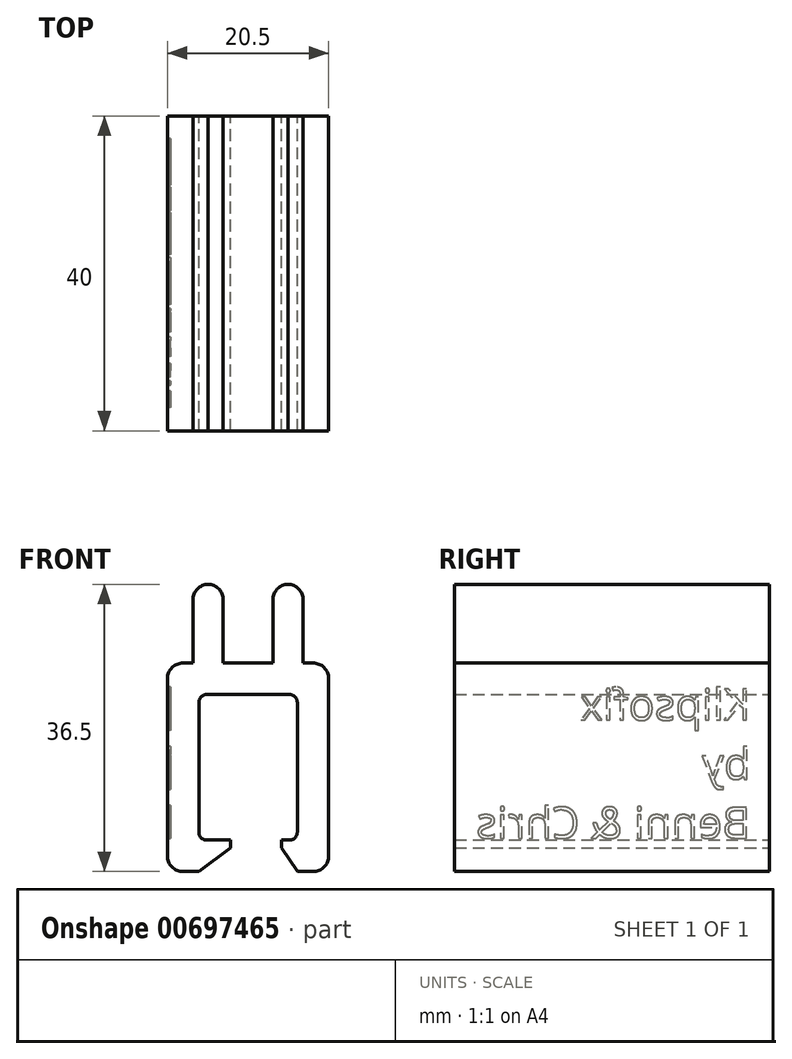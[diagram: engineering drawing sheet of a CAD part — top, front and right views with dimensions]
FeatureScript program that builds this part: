
annotation { "Feature Type Name" : "Feature", "Feature Type Description" : "" }
export const myFeature = defineFeature(function(context is Context, id is Id, definition is map)
    precondition{}
    {
        {
            var Q0;
            Q0=qCreatedBy(makeId("Front.planeOp"),FACE);
            var sketch = newSketch(context, id + "F0", { "sketchPlane" : qUnion([Q0])});
            skLineSegment(sketch, "E0", {"start": v(-16.5, 22.5) * mm, "end": v(-16.5, 4) * mm});
            skLineSegment(sketch, "E1", {"start": v(-16.5, 22.5) * mm, "end": v(-4, 22.5) * mm});
            skLineSegment(sketch, "E2", {"start": v(-4, 22.5) * mm, "end": v(-4, 4) * mm});
            skLineSegment(sketch, "E3", {"start": v(-4, 4) * mm, "end": v(-6, 4) * mm});
            skLineSegment(sketch, "E4", {"start": v(-6, 4) * mm, "end": v(-6, 3) * mm});
            skLineSegment(sketch, "E5", {"start": v(-6, 3) * mm, "end": v(-4, 0) * mm});
            skLineSegment(sketch, "E6", {"start": v(-4, 0) * mm, "end": v(0, 0) * mm});
            skLineSegment(sketch, "E7", {"start": v(0, 0) * mm, "end": v(0, 26.5) * mm});
            skLineSegment(sketch, "E8", {"start": v(0, 26.5) * mm, "end": v(-20.5, 26.5) * mm, "construction": true});
            skLineSegment(sketch, "E9", {"start": v(-20.5, 26.5) * mm, "end": v(-20.5, 0) * mm});
            skLineSegment(sketch, "E10", {"start": v(-20.5, 0) * mm, "end": v(-16.5, 0) * mm});
            skLineSegment(sketch, "E11", {"start": v(-16.5, 4) * mm, "end": v(-12.5, 4) * mm});
            skLineSegment(sketch, "E12", {"start": v(-12.5, 4) * mm, "end": v(-12.5, 3) * mm});
            skLineSegment(sketch, "E13", {"start": v(-12.5, 3) * mm, "end": v(-16.5, 0) * mm});
            skLineSegment(sketch, "E14", {"start": v(-10.25, 26.5) * mm, "end": v(-10.25, 36.5) * mm, "construction": true});
            skLineSegment(sketch, "E15", {"start": v(-13.4, 26.5) * mm, "end": v(-13.4, 36.5) * mm});
            skLineSegment(sketch, "E16", {"start": v(-17.25, 26.5) * mm, "end": v(-17.25, 36.5) * mm});
            skLineSegment(sketch, "E17", {"start": v(-7.1, 26.5) * mm, "end": v(-7.1, 36.5) * mm});
            skLineSegment(sketch, "E18", {"start": v(-3.25, 26.5) * mm, "end": v(-3.25, 36.5) * mm});
            skLineSegment(sketch, "E19", {"start": v(-17.25, 36.5) * mm, "end": v(-13.4, 36.5) * mm});
            skLineSegment(sketch, "E20", {"start": v(-7.1, 36.5) * mm, "end": v(-3.25, 36.5) * mm});
            skLineSegment(sketch, "E21", {"start": v(-13.4, 26.5) * mm, "end": v(-7.1, 26.5) * mm});
            skLineSegment(sketch, "E22", {"start": v(-3.25, 26.5) * mm, "end": v(0, 26.5) * mm});
            skLineSegment(sketch, "E23", {"start": v(-20.5, 26.5) * mm, "end": v(-17.25, 26.5) * mm});
            skSolve(sketch);
        }
        {
            var Q0;
            Q0 = qSketchRegion(id + "F0", true);
            extrude(context, id + "F1", {"entities" : qUnion([Q0]), "depth" : 40 * mm, "offsetDistance" : 25 * mm});
        }
        {
            var Q0;
            Q0=makeQuery(id+"F1.opExtrude","SWEPT_EDGE",EDGE,{"disambiguationData":[OSD([sQuery(id+"F0.wireOp",EDGE,"E7"),sQuery(id+"F0.wireOp",EDGE,"E22")])]});
            var Q1;
            Q1=makeQuery(id+"F1.opExtrude","SWEPT_EDGE",EDGE,{"disambiguationData":[OSD([sQuery(id+"F0.wireOp",EDGE,"E6"),sQuery(id+"F0.wireOp",EDGE,"E7")])]});
            var Q2;
            Q2=makeQuery(id+"F1.opExtrude","SWEPT_EDGE",EDGE,{"disambiguationData":[OSD([sQuery(id+"F0.wireOp",EDGE,"E9"),sQuery(id+"F0.wireOp",EDGE,"E23")])]});
            var Q3;
            Q3=makeQuery(id+"F1.opExtrude","SWEPT_EDGE",EDGE,{"disambiguationData":[OSD([sQuery(id+"F0.wireOp",EDGE,"E9"),sQuery(id+"F0.wireOp",EDGE,"E10")])]});
            fillet(context, id + "F2", {"entities" : qUnion([Q0, Q1, Q2, Q3]), "radius" : 2 * mm, "tangentPropagation" : true, "allowEdgeOverflow" : false});
        }
        {
            var Q0;
            Q0=makeQuery(id+"F1.opExtrude","SWEPT_EDGE",EDGE,{"disambiguationData":[OSD([sQuery(id+"F0.wireOp",EDGE,"E18"),sQuery(id+"F0.wireOp",EDGE,"E20")])]});
            var Q1;
            Q1=makeQuery(id+"F1.opExtrude","SWEPT_EDGE",EDGE,{"disambiguationData":[OSD([sQuery(id+"F0.wireOp",EDGE,"E16"),sQuery(id+"F0.wireOp",EDGE,"E19")])]});
            var Q2;
            Q2=makeQuery(id+"F1.opExtrude","SWEPT_EDGE",EDGE,{"disambiguationData":[OSD([sQuery(id+"F0.wireOp",EDGE,"E17"),sQuery(id+"F0.wireOp",EDGE,"E20")])]});
            var Q3;
            Q3=makeQuery(id+"F1.opExtrude","SWEPT_EDGE",EDGE,{"disambiguationData":[OSD([sQuery(id+"F0.wireOp",EDGE,"E15"),sQuery(id+"F0.wireOp",EDGE,"E19")])]});
            fillet(context, id + "F3", {"entities" : qUnion([Q0, Q1, Q2, Q3]), "radius" : 2 * mm, "tangentPropagation" : true, "allowEdgeOverflow" : false});
        }
        {
            var Q0;
            Q0=makeQuery(id+"F1.opExtrude","SWEPT_EDGE",EDGE,{"disambiguationData":[OSD([sQuery(id+"F0.wireOp",EDGE,"E0"),sQuery(id+"F0.wireOp",EDGE,"E1")])]});
            var Q1;
            Q1=makeQuery(id+"F1.opExtrude","SWEPT_EDGE",EDGE,{"disambiguationData":[OSD([sQuery(id+"F0.wireOp",EDGE,"E1"),sQuery(id+"F0.wireOp",EDGE,"E2")])]});
            var Q2;
            Q2=makeQuery(id+"F1.opExtrude","SWEPT_EDGE",EDGE,{"disambiguationData":[OSD([sQuery(id+"F0.wireOp",EDGE,"E0"),sQuery(id+"F0.wireOp",EDGE,"E11")])]});
            var Q3;
            Q3=makeQuery(id+"F1.opExtrude","SWEPT_EDGE",EDGE,{"disambiguationData":[OSD([sQuery(id+"F0.wireOp",EDGE,"E2"),sQuery(id+"F0.wireOp",EDGE,"E3")])]});
            fillet(context, id + "F4", {"entities" : qUnion([Q0, Q1, Q2, Q3]), "radius" : 1 * mm, "tangentPropagation" : true, "allowEdgeOverflow" : false});
        }
        {
            var Q0;
            Q0=makeQuery(id+"F1.opExtrude","SWEPT_FACE",FACE,{"disambiguationData":[OSD([sQuery(id+"F0.wireOp",EDGE,"E9")])]});
            var sketch = newSketch(context, id + "F5", { "sketchPlane" : qUnion([Q0])});
            skText(sketch, "E24", { "text": "Klipsofix \nby \nBenni & Chris", "fontName": "OpenSans-Regular.ttf"});
            const initialGuessF5  = {"E24": [0.00242, 0.01924, 1, 0, 0.00397]};
            skSetInitialGuess(sketch, initialGuessF5);
            skSolve(sketch);
        }
        {
            var Q0;
            Q0 = qSketchRegion(id + "F5", true);
            extrude(context, id + "F6", {"entities" : qUnion([Q0]), "operationType" : NewBodyOperationType.REMOVE, "oppositeDirection" : true, "depth" : 0.4 * mm, "offsetDistance" : 25 * mm});
        }
    });
